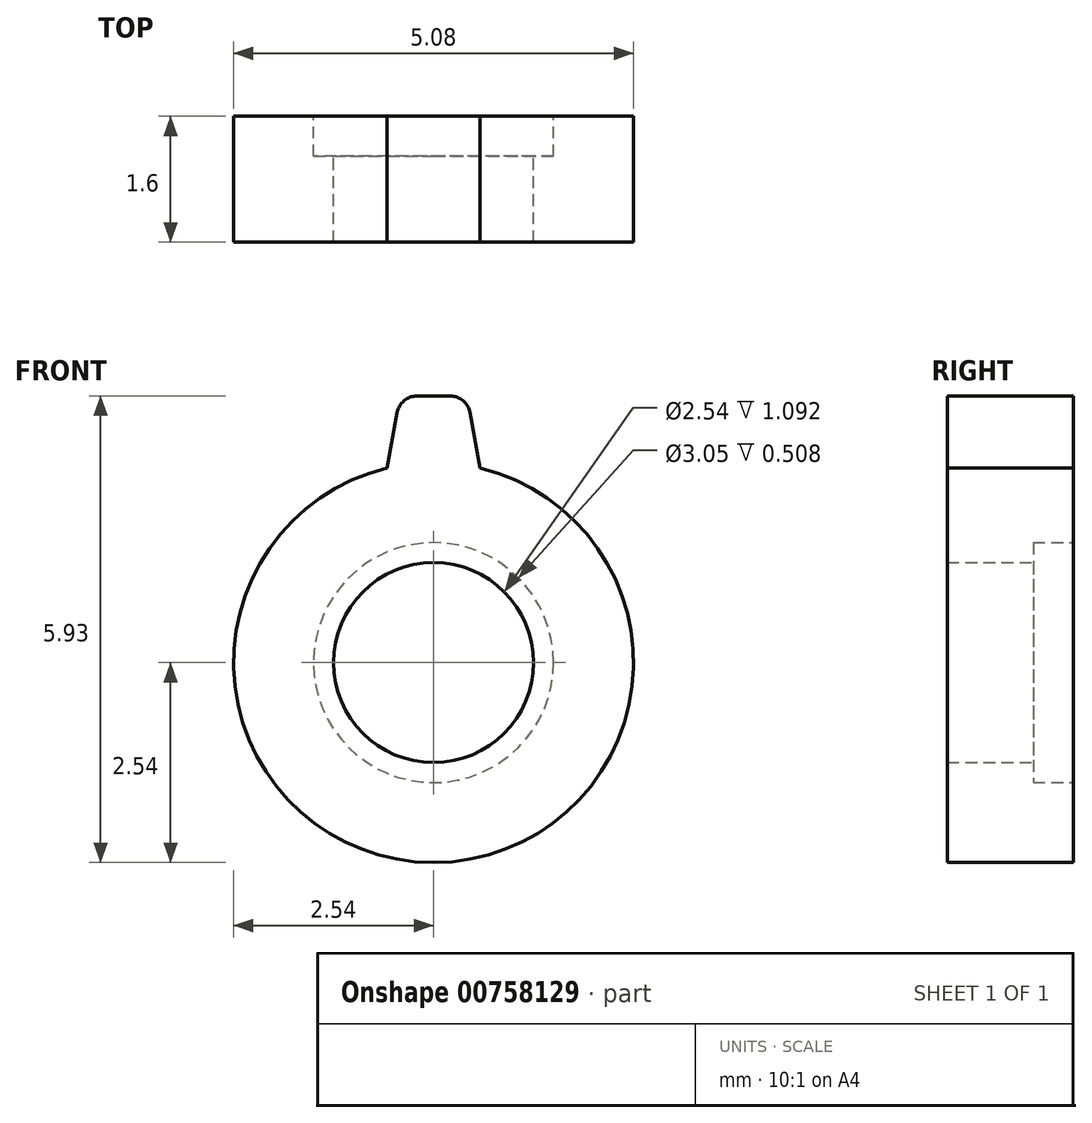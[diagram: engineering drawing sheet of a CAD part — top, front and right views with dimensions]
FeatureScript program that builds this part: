
annotation { "Feature Type Name" : "Feature", "Feature Type Description" : "" }
export const myFeature = defineFeature(function(context is Context, id is Id, definition is map)
    precondition{}
    {
        {
            var Q0;
            Q0=qCreatedBy(makeId("Front.planeOp"),FACE);
            var sketch = newSketch(context, id + "F0", { "sketchPlane" : qUnion([Q0])});
            skCircle(sketch, "E0", {"center": v(0, 0) * mm, "radius": 1.27 * mm});
            skCircle(sketch, "E1", {"center": v(0, 0) * mm, "radius": 2.54 * mm});
            skSolve(sketch);
        }
        {
            var Q0;
            Q0 = qSketchRegion(id + "F0", true);
            extrude(context, id + "F1", {"entities" : qUnion([Q0]), "depth" : 1.6 * mm, "offsetDistance" : 25.4 * mm});
        }
        {
            var Q0;
            Q0=makeQuery(id+"F1.opExtrude","CAP_FACE",FACE,{"disambiguationData":[OSD([sQuery(id+"F0.wireOp",EDGE,"E0"),sQuery(id+"F0.wireOp",EDGE,"E1")])],"isStart":false});
            var sketch = newSketch(context, id + "F2", { "sketchPlane" : qUnion([Q0])});
            skLineSegment(sketch, "E2.top", {"start": v(-0.42, 3.39) * mm, "end": v(0.42, 3.39) * mm});
            skLineSegment(sketch, "E3", {"start": v(-0.42, 3.39) * mm, "end": v(-0.6, 2.47) * mm});
            skLineSegment(sketch, "E4", {"start": v(0.42, 3.39) * mm, "end": v(0.6, 2.47) * mm});
            skLineSegment(sketch, "E5", {"start": v(-0.6, 2.47) * mm, "end": v(0.6, 2.47) * mm});
            skSolve(sketch);
        }
        {
            var Q0;
            Q0 = qSketchRegion(id + "F2", true);
            var Q1;
            Q1=makeQuery(id+"F1.opExtrude","CAP_FACE",FACE,{"disambiguationData":[OSD([sQuery(id+"F0.wireOp",EDGE,"E0"),sQuery(id+"F0.wireOp",EDGE,"E1")])],"isStart":true});
            extrude(context, id + "F3", {"entities" : qUnion([Q0]), "operationType" : NewBodyOperationType.ADD, "endBound" : BoundingType.UP_TO_SURFACE, "oppositeDirection" : true, "depth" : 25.4 * mm, "endBoundEntityFace" : qUnion([Q1]), "offsetDistance" : 25.4 * mm});
        }
        {
            var Q0;
            Q0=qCreatedBy(makeId("Top.planeOp"),FACE);
            var sketch = newSketch(context, id + "F4", { "sketchPlane" : qUnion([Q0])});
            skLineSegment(sketch, "E6", {"start": v(0, 1.9) * mm, "end": v(0, -7.18) * mm});
            skSolve(sketch);
        }
        {
            var Q0;
            Q0=makeQuery(id+"F7Nf8V9IbyF9cH7_1.1.F3.opExtrude","SWEPT_EDGE",EDGE,{"disambiguationData":[OSD([sQuery(id+"F2.wireOp",EDGE,"E2.top"),sQuery(id+"F2.wireOp",EDGE,"E4")])]});
            var Q1;
            Q1=makeQuery(id+"F7Nf8V9IbyF9cH7_1.1.F3.opExtrude","SWEPT_EDGE",EDGE,{"disambiguationData":[OSD([sQuery(id+"F2.wireOp",EDGE,"E2.top"),sQuery(id+"F2.wireOp",EDGE,"E3")])]});
            var Q2;
            Q2=makeQuery(id+"F3.opExtrude","SWEPT_EDGE",EDGE,{"disambiguationData":[OSD([sQuery(id+"F2.wireOp",EDGE,"E2.top"),sQuery(id+"F2.wireOp",EDGE,"E3")])]});
            var Q3;
            Q3=makeQuery(id+"F7Nf8V9IbyF9cH7_1.1.F3.opExtrude","SWEPT_EDGE",EDGE,{"disambiguationData":[OSD([sQuery(id+"F0.wireOp",EDGE,"E1"),sQuery(id+"F2.wireOp",EDGE,"E4"),sQuery(id+"F2.wireOp",EDGE,"E5")])]});
            var Q4;
            Q4=makeQuery(id+"F3.opExtrude","SWEPT_EDGE",EDGE,{"disambiguationData":[OSD([sQuery(id+"F0.wireOp",EDGE,"E1"),sQuery(id+"F2.wireOp",EDGE,"E3"),sQuery(id+"F2.wireOp",EDGE,"E5")])]});
            var Q5;
            Q5=makeQuery(id+"F3.opExtrude","SWEPT_EDGE",EDGE,{"disambiguationData":[OSD([sQuery(id+"F2.wireOp",EDGE,"E2.top"),sQuery(id+"F2.wireOp",EDGE,"E4")])]});
            var Q6;
            Q6=makeQuery(id+"F3.opExtrude","SWEPT_EDGE",EDGE,{"disambiguationData":[OSD([sQuery(id+"F0.wireOp",EDGE,"E1"),sQuery(id+"F2.wireOp",EDGE,"E4"),sQuery(id+"F2.wireOp",EDGE,"E5")])]});
            var Q7;
            Q7=makeQuery(id+"F7Nf8V9IbyF9cH7_1.7.F3.opExtrude","SWEPT_EDGE",EDGE,{"disambiguationData":[OSD([sQuery(id+"F0.wireOp",EDGE,"E1"),sQuery(id+"F2.wireOp",EDGE,"E3"),sQuery(id+"F2.wireOp",EDGE,"E5")])]});
            var Q8;
            Q8=makeQuery(id+"F7Nf8V9IbyF9cH7_1.7.F3.opExtrude","SWEPT_EDGE",EDGE,{"disambiguationData":[OSD([sQuery(id+"F2.wireOp",EDGE,"E2.top"),sQuery(id+"F2.wireOp",EDGE,"E3")])]});
            var Q9;
            Q9=makeQuery(id+"F7Nf8V9IbyF9cH7_1.7.F3.opExtrude","SWEPT_EDGE",EDGE,{"disambiguationData":[OSD([sQuery(id+"F2.wireOp",EDGE,"E2.top"),sQuery(id+"F2.wireOp",EDGE,"E4")])]});
            var Q10;
            Q10=makeQuery(id+"F7Nf8V9IbyF9cH7_1.7.F3.opExtrude","SWEPT_EDGE",EDGE,{"disambiguationData":[OSD([sQuery(id+"F0.wireOp",EDGE,"E1"),sQuery(id+"F2.wireOp",EDGE,"E4"),sQuery(id+"F2.wireOp",EDGE,"E5")])]});
            var Q11;
            Q11=makeQuery(id+"F7Nf8V9IbyF9cH7_1.6.F3.opExtrude","SWEPT_EDGE",EDGE,{"disambiguationData":[OSD([sQuery(id+"F0.wireOp",EDGE,"E1"),sQuery(id+"F2.wireOp",EDGE,"E3"),sQuery(id+"F2.wireOp",EDGE,"E5")])]});
            var Q12;
            Q12=makeQuery(id+"F7Nf8V9IbyF9cH7_1.6.F3.opExtrude","SWEPT_EDGE",EDGE,{"disambiguationData":[OSD([sQuery(id+"F2.wireOp",EDGE,"E2.top"),sQuery(id+"F2.wireOp",EDGE,"E3")])]});
            var Q13;
            Q13=makeQuery(id+"F7Nf8V9IbyF9cH7_1.6.F3.opExtrude","SWEPT_EDGE",EDGE,{"disambiguationData":[OSD([sQuery(id+"F2.wireOp",EDGE,"E2.top"),sQuery(id+"F2.wireOp",EDGE,"E4")])]});
            var Q14;
            Q14=makeQuery(id+"F7Nf8V9IbyF9cH7_1.6.F3.opExtrude","SWEPT_EDGE",EDGE,{"disambiguationData":[OSD([sQuery(id+"F0.wireOp",EDGE,"E1"),sQuery(id+"F2.wireOp",EDGE,"E4"),sQuery(id+"F2.wireOp",EDGE,"E5")])]});
            var Q15;
            Q15=makeQuery(id+"F7Nf8V9IbyF9cH7_1.5.F3.opExtrude","SWEPT_EDGE",EDGE,{"disambiguationData":[OSD([sQuery(id+"F0.wireOp",EDGE,"E1"),sQuery(id+"F2.wireOp",EDGE,"E3"),sQuery(id+"F2.wireOp",EDGE,"E5")])]});
            var Q16;
            Q16=makeQuery(id+"F7Nf8V9IbyF9cH7_1.5.F3.opExtrude","SWEPT_EDGE",EDGE,{"disambiguationData":[OSD([sQuery(id+"F2.wireOp",EDGE,"E2.top"),sQuery(id+"F2.wireOp",EDGE,"E3")])]});
            var Q17;
            Q17=makeQuery(id+"F7Nf8V9IbyF9cH7_1.5.F3.opExtrude","SWEPT_EDGE",EDGE,{"disambiguationData":[OSD([sQuery(id+"F2.wireOp",EDGE,"E2.top"),sQuery(id+"F2.wireOp",EDGE,"E4")])]});
            var Q18;
            Q18=makeQuery(id+"F7Nf8V9IbyF9cH7_1.5.F3.opExtrude","SWEPT_EDGE",EDGE,{"disambiguationData":[OSD([sQuery(id+"F0.wireOp",EDGE,"E1"),sQuery(id+"F2.wireOp",EDGE,"E4"),sQuery(id+"F2.wireOp",EDGE,"E5")])]});
            var Q19;
            Q19=makeQuery(id+"F7Nf8V9IbyF9cH7_1.4.F3.opExtrude","SWEPT_EDGE",EDGE,{"disambiguationData":[OSD([sQuery(id+"F0.wireOp",EDGE,"E1"),sQuery(id+"F2.wireOp",EDGE,"E3"),sQuery(id+"F2.wireOp",EDGE,"E5")])]});
            var Q20;
            Q20=makeQuery(id+"F7Nf8V9IbyF9cH7_1.4.F3.opExtrude","SWEPT_EDGE",EDGE,{"disambiguationData":[OSD([sQuery(id+"F2.wireOp",EDGE,"E2.top"),sQuery(id+"F2.wireOp",EDGE,"E3")])]});
            var Q21;
            Q21=makeQuery(id+"F7Nf8V9IbyF9cH7_1.4.F3.opExtrude","SWEPT_EDGE",EDGE,{"disambiguationData":[OSD([sQuery(id+"F2.wireOp",EDGE,"E2.top"),sQuery(id+"F2.wireOp",EDGE,"E4")])]});
            var Q22;
            Q22=makeQuery(id+"F7Nf8V9IbyF9cH7_1.4.F3.opExtrude","SWEPT_EDGE",EDGE,{"disambiguationData":[OSD([sQuery(id+"F0.wireOp",EDGE,"E1"),sQuery(id+"F2.wireOp",EDGE,"E4"),sQuery(id+"F2.wireOp",EDGE,"E5")])]});
            var Q23;
            Q23=makeQuery(id+"F7Nf8V9IbyF9cH7_1.3.F3.opExtrude","SWEPT_EDGE",EDGE,{"disambiguationData":[OSD([sQuery(id+"F0.wireOp",EDGE,"E1"),sQuery(id+"F2.wireOp",EDGE,"E3"),sQuery(id+"F2.wireOp",EDGE,"E5")])]});
            var Q24;
            Q24=makeQuery(id+"F7Nf8V9IbyF9cH7_1.3.F3.opExtrude","SWEPT_EDGE",EDGE,{"disambiguationData":[OSD([sQuery(id+"F2.wireOp",EDGE,"E2.top"),sQuery(id+"F2.wireOp",EDGE,"E3")])]});
            var Q25;
            Q25=makeQuery(id+"F7Nf8V9IbyF9cH7_1.3.F3.opExtrude","SWEPT_EDGE",EDGE,{"disambiguationData":[OSD([sQuery(id+"F0.wireOp",EDGE,"E1"),sQuery(id+"F2.wireOp",EDGE,"E4"),sQuery(id+"F2.wireOp",EDGE,"E5")])]});
            var Q26;
            Q26=makeQuery(id+"F7Nf8V9IbyF9cH7_1.2.F3.opExtrude","SWEPT_EDGE",EDGE,{"disambiguationData":[OSD([sQuery(id+"F0.wireOp",EDGE,"E1"),sQuery(id+"F2.wireOp",EDGE,"E3"),sQuery(id+"F2.wireOp",EDGE,"E5")])]});
            var Q27;
            Q27=makeQuery(id+"F7Nf8V9IbyF9cH7_1.3.F3.opExtrude","SWEPT_EDGE",EDGE,{"disambiguationData":[OSD([sQuery(id+"F2.wireOp",EDGE,"E2.top"),sQuery(id+"F2.wireOp",EDGE,"E4")])]});
            var Q28;
            Q28=makeQuery(id+"F7Nf8V9IbyF9cH7_1.2.F3.opExtrude","SWEPT_EDGE",EDGE,{"disambiguationData":[OSD([sQuery(id+"F2.wireOp",EDGE,"E2.top"),sQuery(id+"F2.wireOp",EDGE,"E3")])]});
            var Q29;
            Q29=makeQuery(id+"F7Nf8V9IbyF9cH7_1.2.F3.opExtrude","SWEPT_EDGE",EDGE,{"disambiguationData":[OSD([sQuery(id+"F2.wireOp",EDGE,"E2.top"),sQuery(id+"F2.wireOp",EDGE,"E4")])]});
            var Q30;
            Q30=makeQuery(id+"F7Nf8V9IbyF9cH7_1.1.F3.opExtrude","SWEPT_EDGE",EDGE,{"disambiguationData":[OSD([sQuery(id+"F0.wireOp",EDGE,"E1"),sQuery(id+"F2.wireOp",EDGE,"E3"),sQuery(id+"F2.wireOp",EDGE,"E5")])]});
            var Q31;
            Q31=makeQuery(id+"F7Nf8V9IbyF9cH7_1.2.F3.opExtrude","SWEPT_EDGE",EDGE,{"disambiguationData":[OSD([sQuery(id+"F0.wireOp",EDGE,"E1"),sQuery(id+"F2.wireOp",EDGE,"E4"),sQuery(id+"F2.wireOp",EDGE,"E5")])]});
            fillet(context, id + "F5", {"entities" : qUnion([Q0, Q1, Q2, Q3, Q4, Q5, Q6, Q7, Q8, Q9, Q10, Q11, Q12, Q13, Q14, Q15, Q16, Q17, Q18, Q19, Q20, Q21, Q22, Q23, Q24, Q25, Q26, Q27, Q28, Q29, Q30, Q31]), "radius" : 0.25 * mm, "tangentPropagation" : true, "allowEdgeOverflow" : false});
        }
        {
            var Q0;
            {var subQ0=sQuery(id+"F0.wireOp",EDGE,"E1");var subQ1=sQuery(id+"F0.wireOp",EDGE,"E0");Q0=makeQuery(id+"F7Nf8V9IbyF9cH7_1.7.F3.boolean.opBoolean","MERGE",FACE,{"derivedFrom":[makeQuery(id+"F7Nf8V9IbyF9cH7_1.6.F3.boolean.opBoolean","MERGE",FACE,{"derivedFrom":[makeQuery(id+"F7Nf8V9IbyF9cH7_1.5.F3.boolean.opBoolean","MERGE",FACE,{"derivedFrom":[makeQuery(id+"F7Nf8V9IbyF9cH7_1.4.F3.boolean.opBoolean","MERGE",FACE,{"derivedFrom":[makeQuery(id+"F7Nf8V9IbyF9cH7_1.3.F3.boolean.opBoolean","MERGE",FACE,{"derivedFrom":[makeQuery(id+"F7Nf8V9IbyF9cH7_1.2.F3.boolean.opBoolean","MERGE",FACE,{"derivedFrom":[makeQuery(id+"F7Nf8V9IbyF9cH7_1.1.F3.boolean.opBoolean","MERGE",FACE,{"derivedFrom":[makeQuery(id+"F3.boolean.opBoolean","MERGE",FACE,{"derivedFrom":[makeQuery(id+"F1.opExtrude","CAP_FACE",FACE,{"disambiguationData":[OSD([subQ1,subQ0])],"isStart":true}),makeQuery(id+"F3.opExtrude","CAP_FACE",FACE,{"disambiguationData":[OSD([subQ1,subQ0])],"isStart":false})]}),makeQuery(id+"F7Nf8V9IbyF9cH7_1.1.F3.opExtrude","CAP_FACE",FACE,{"disambiguationData":[OSD([subQ1,subQ0])],"isStart":false})]}),makeQuery(id+"F7Nf8V9IbyF9cH7_1.2.F3.opExtrude","CAP_FACE",FACE,{"disambiguationData":[OSD([subQ1,subQ0])],"isStart":false})]}),makeQuery(id+"F7Nf8V9IbyF9cH7_1.3.F3.opExtrude","CAP_FACE",FACE,{"disambiguationData":[OSD([subQ1,subQ0])],"isStart":false})]}),makeQuery(id+"F7Nf8V9IbyF9cH7_1.4.F3.opExtrude","CAP_FACE",FACE,{"disambiguationData":[OSD([subQ1,subQ0])],"isStart":false})]}),makeQuery(id+"F7Nf8V9IbyF9cH7_1.5.F3.opExtrude","CAP_FACE",FACE,{"disambiguationData":[OSD([subQ1,subQ0])],"isStart":false})]}),makeQuery(id+"F7Nf8V9IbyF9cH7_1.6.F3.opExtrude","CAP_FACE",FACE,{"disambiguationData":[OSD([subQ1,subQ0])],"isStart":false})]}),makeQuery(id+"F7Nf8V9IbyF9cH7_1.7.F3.opExtrude","CAP_FACE",FACE,{"disambiguationData":[OSD([subQ1,subQ0])],"isStart":false})]});}
            var sketch = newSketch(context, id + "F6", { "sketchPlane" : qUnion([Q0])});
            skCircle(sketch, "E7", {"center": v(0, 0) * mm, "radius": 1.52 * mm});
            skSolve(sketch);
        }
        {
            var Q0;
            Q0 = qSketchRegion(id + "F6", true);
            extrude(context, id + "F7", {"entities" : qUnion([Q0]), "operationType" : NewBodyOperationType.REMOVE, "oppositeDirection" : true, "depth" : 0.5 * mm, "offsetDistance" : 25.4 * mm});
        }
    });
